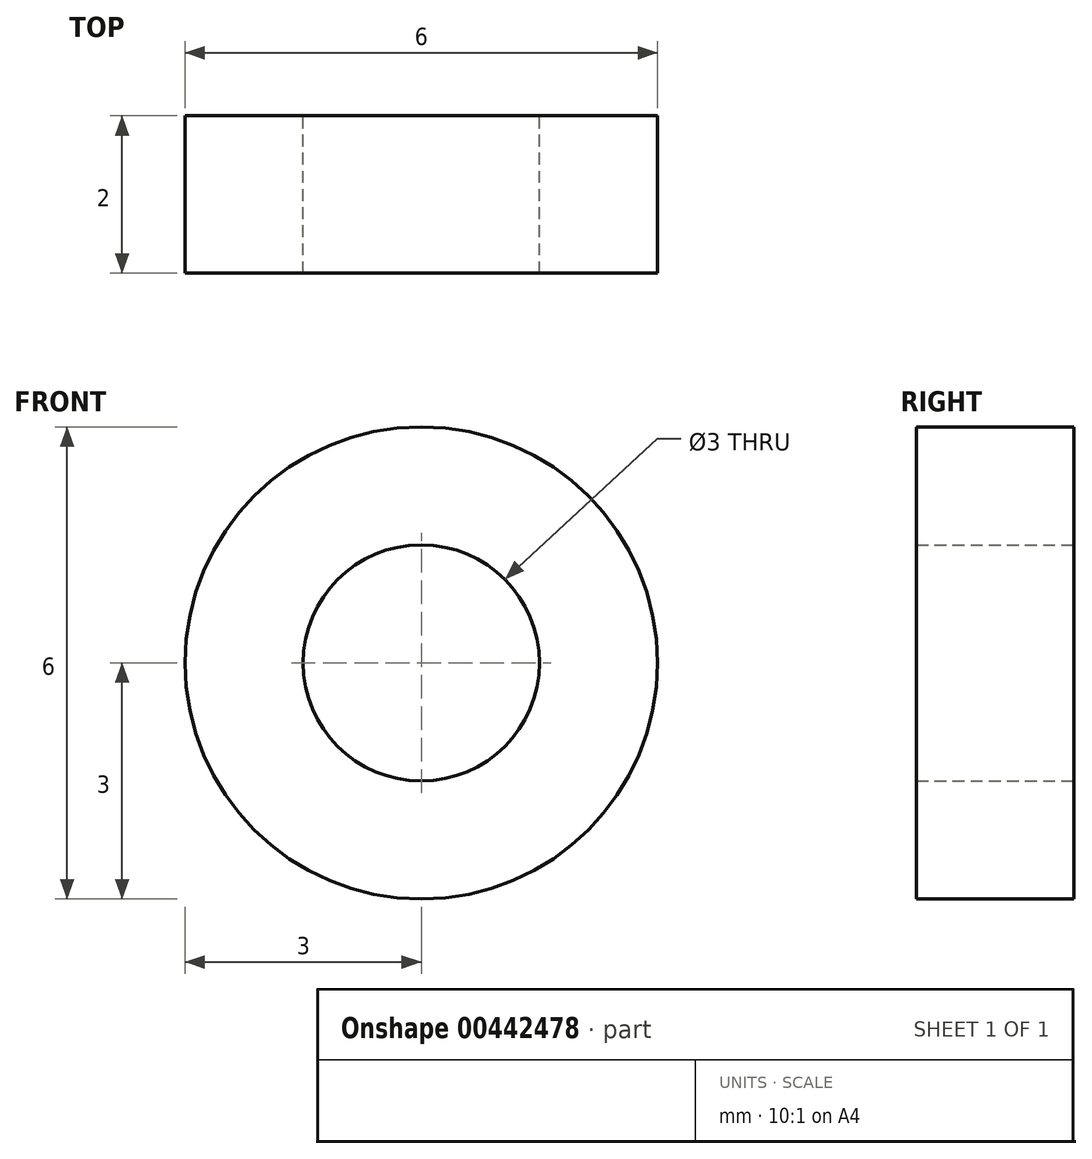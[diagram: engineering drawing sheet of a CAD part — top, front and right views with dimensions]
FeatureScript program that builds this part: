
annotation { "Feature Type Name" : "Feature", "Feature Type Description" : "" }
export const myFeature = defineFeature(function(context is Context, id is Id, definition is map)
    precondition{}
    {
        {
            var Q0;
            Q0=qCreatedBy(makeId("Front.planeOp"),FACE);
            var sketch = newSketch(context, id + "F0", { "sketchPlane" : qUnion([Q0])});
            skCircle(sketch, "E0", {"center": v(0, 0) * mm, "radius": 1.5 * mm});
            skCircle(sketch, "E1", {"center": v(0, 0) * mm, "radius": 3 * mm});
            skSolve(sketch);
        }
        {
            var Q0;
            Q0=qSketchRegion(id+"F0",true);
            extrude(context, id + "F1", {"entities" : qUnion([Q0]), "depth" : 2 * mm});
        }
    });
